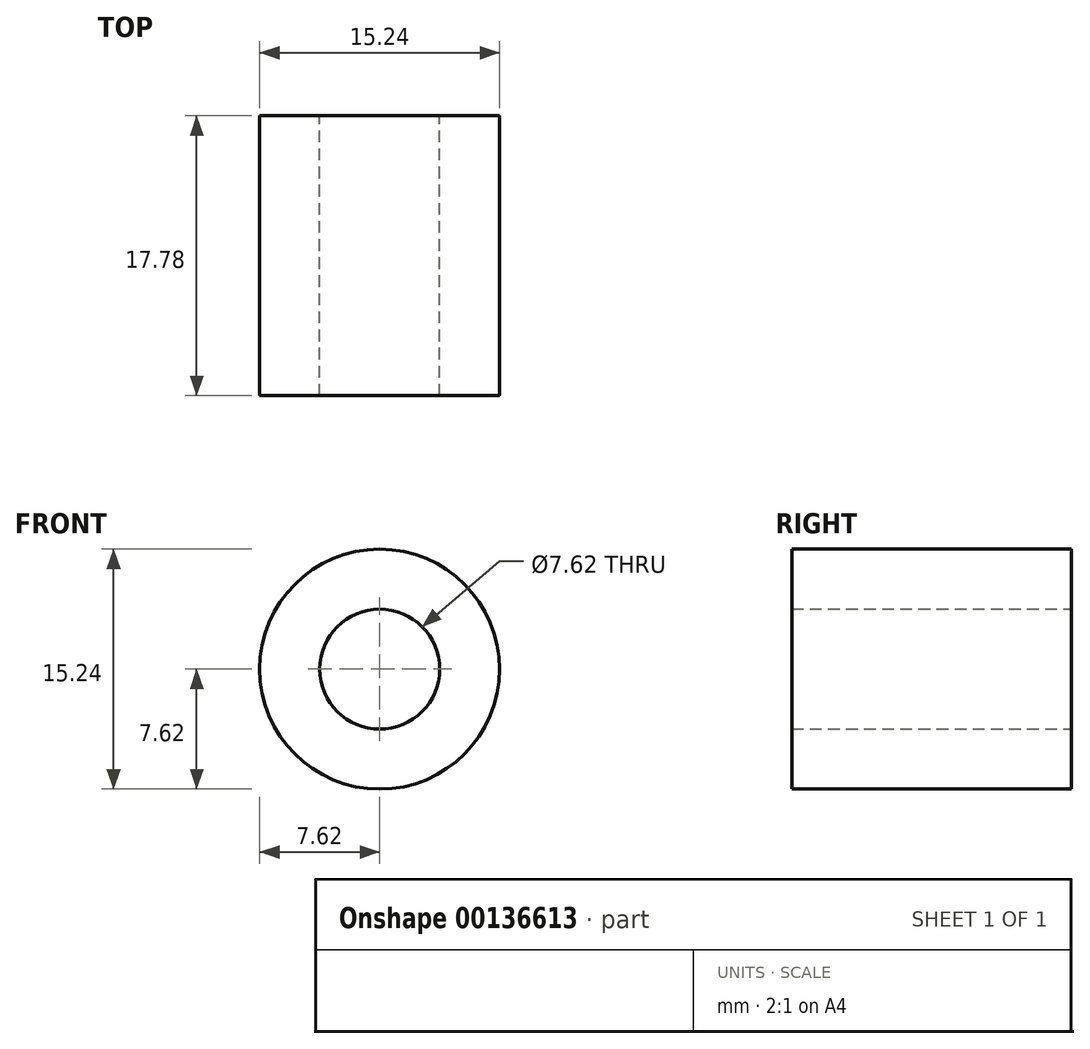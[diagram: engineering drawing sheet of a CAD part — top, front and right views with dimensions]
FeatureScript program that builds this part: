
annotation { "Feature Type Name" : "Feature", "Feature Type Description" : "" }
export const myFeature = defineFeature(function(context is Context, id is Id, definition is map)
    precondition{}
    {
        {
            var Q0;
            Q0=qCreatedBy(makeId("Front.planeOp"),FACE);
            var sketch = newSketch(context, id + "F0", { "sketchPlane" : qUnion([Q0])});
            skCircle(sketch, "E0", {"center": v(0, 0) * mm, "radius": 7.62 * mm});
            skCircle(sketch, "E1", {"center": v(0, 0) * mm, "radius": 3.81 * mm});
            skSolve(sketch);
        }
        {
            var Q0;
            Q0=makeQuery(id+"F0.imprint","IMPRINT",FACE,{"disambiguationData":[TD([[makeQuery(id+"F0.imprint","IMPRINT",EDGE,{"derivedFrom":sQuery(id+"F0.wireOp",EDGE,"E0")}),1.0]])]});
            extrude(context, id + "F1", {"entities" : qUnion([Q0]), "depth" : 17.78 * mm});
        }
    });
